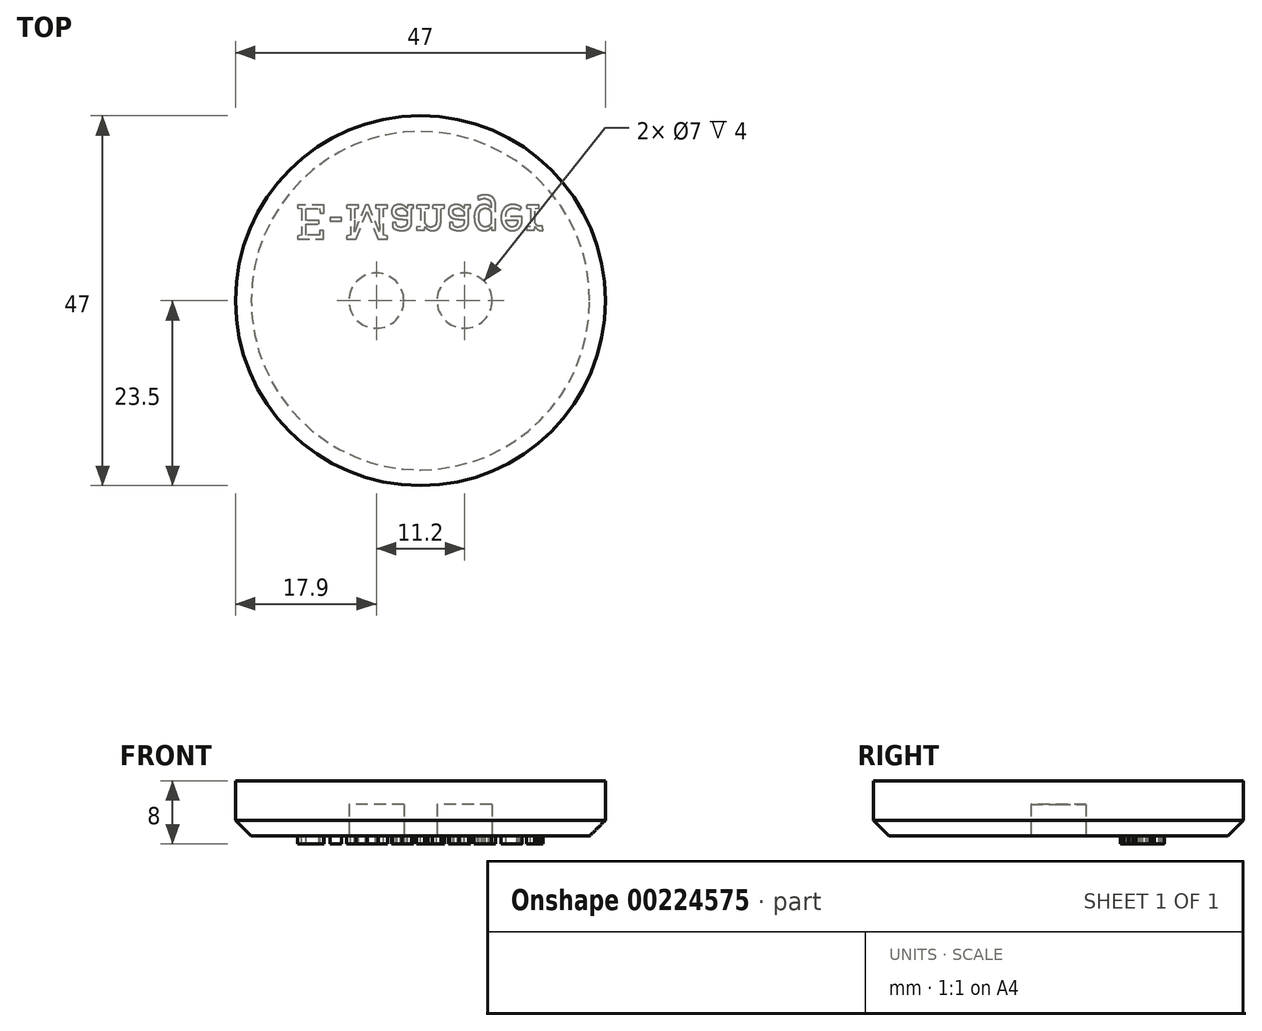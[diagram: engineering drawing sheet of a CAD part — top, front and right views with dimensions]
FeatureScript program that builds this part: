
annotation { "Feature Type Name" : "Feature", "Feature Type Description" : "" }
export const myFeature = defineFeature(function(context is Context, id is Id, definition is map)
    precondition{}
    {
        {
            var Q0;
            Q0=qCreatedBy(makeId("Top.planeOp"),FACE);
            var sketch = newSketch(context, id + "F0", { "sketchPlane" : qUnion([Q0])});
            skCircle(sketch, "E0", {"center": v(0, 0) * mm, "radius": 23.5 * mm});
            skSolve(sketch);
        }
        {
            var Q0;
            Q0=makeQuery(id+"F0.imprint","IMPRINT",FACE,{"disambiguationData":[TD([[makeQuery(id+"F0.imprint","IMPRINT",EDGE,{"derivedFrom":sQuery(id+"F0.wireOp",EDGE,"E0")}),1.0]])]});
            extrude(context, id + "F1", {"entities" : qUnion([Q0]), "depth" : 7 * mm});
        }
        {
            var Q0;
            Q0=qCreatedBy(makeId("Top.planeOp"),FACE);
            var sketch = newSketch(context, id + "F2", { "sketchPlane" : qUnion([Q0])});
            skLineSegment(sketch, "E1", {"start": v(-5.6, 0) * mm, "end": v(5.6, 0) * mm, "construction": true});
            skCircle(sketch, "E2", {"center": v(-5.6, 0) * mm, "radius": 3.5 * mm});
            skCircle(sketch, "E3", {"center": v(5.6, 0) * mm, "radius": 3.5 * mm});
            skSolve(sketch);
        }
        {
            var Q0;
            Q0=makeQuery(id+"F2.imprint","IMPRINT",FACE,{"disambiguationData":[TD([[makeQuery(id+"F2.imprint","IMPRINT",EDGE,{"derivedFrom":sQuery(id+"F2.wireOp",EDGE,"E3")}),1.0]])]});
            var Q1;
            Q1=makeQuery(id+"F2.imprint","IMPRINT",FACE,{"disambiguationData":[TD([[makeQuery(id+"F2.imprint","IMPRINT",EDGE,{"derivedFrom":sQuery(id+"F2.wireOp",EDGE,"E2")}),1.0]])]});
            extrude(context, id + "F3", {"entities" : qUnion([Q0, Q1]), "operationType" : NewBodyOperationType.REMOVE, "depth" : 4 * mm});
        }
        {
            var Q0;
            Q0=makeQuery(id+"F1.opExtrude","CAP_EDGE",EDGE,{"disambiguationData":[OSD([sQuery(id+"F0.wireOp",EDGE,"E0")])],"isStart":true});
            chamfer(context, id + "F4", {"entities" : qUnion([Q0]), "width" : 2 * mm, "tangentPropagation" : true});
        }
        {
            var Q0;
            Q0=makeQuery(id+"F1.opExtrude","CAP_FACE",FACE,{"disambiguationData":[OSD([sQuery(id+"F0.wireOp",EDGE,"E0")])],"isStart":true});
            var sketch = newSketch(context, id + "F5", { "sketchPlane" : qUnion([Q0])});
            skText(sketch, "E4", { "text": "E-Manager", "fontName": "RobotoSlab-Regular.ttf"});
            const initialGuessF5  = {"E4": [-0.0158, -0.01215, 1, 0, 0.00435]};
            skSetInitialGuess(sketch, initialGuessF5);
            skSolve(sketch);
        }
        {
            var Q0;
            Q0 = qSketchRegion(id + "F5", true);
            extrude(context, id + "F6", {"entities" : qUnion([Q0]), "operationType" : NewBodyOperationType.ADD, "depth" : 1 * mm});
        }
    });
